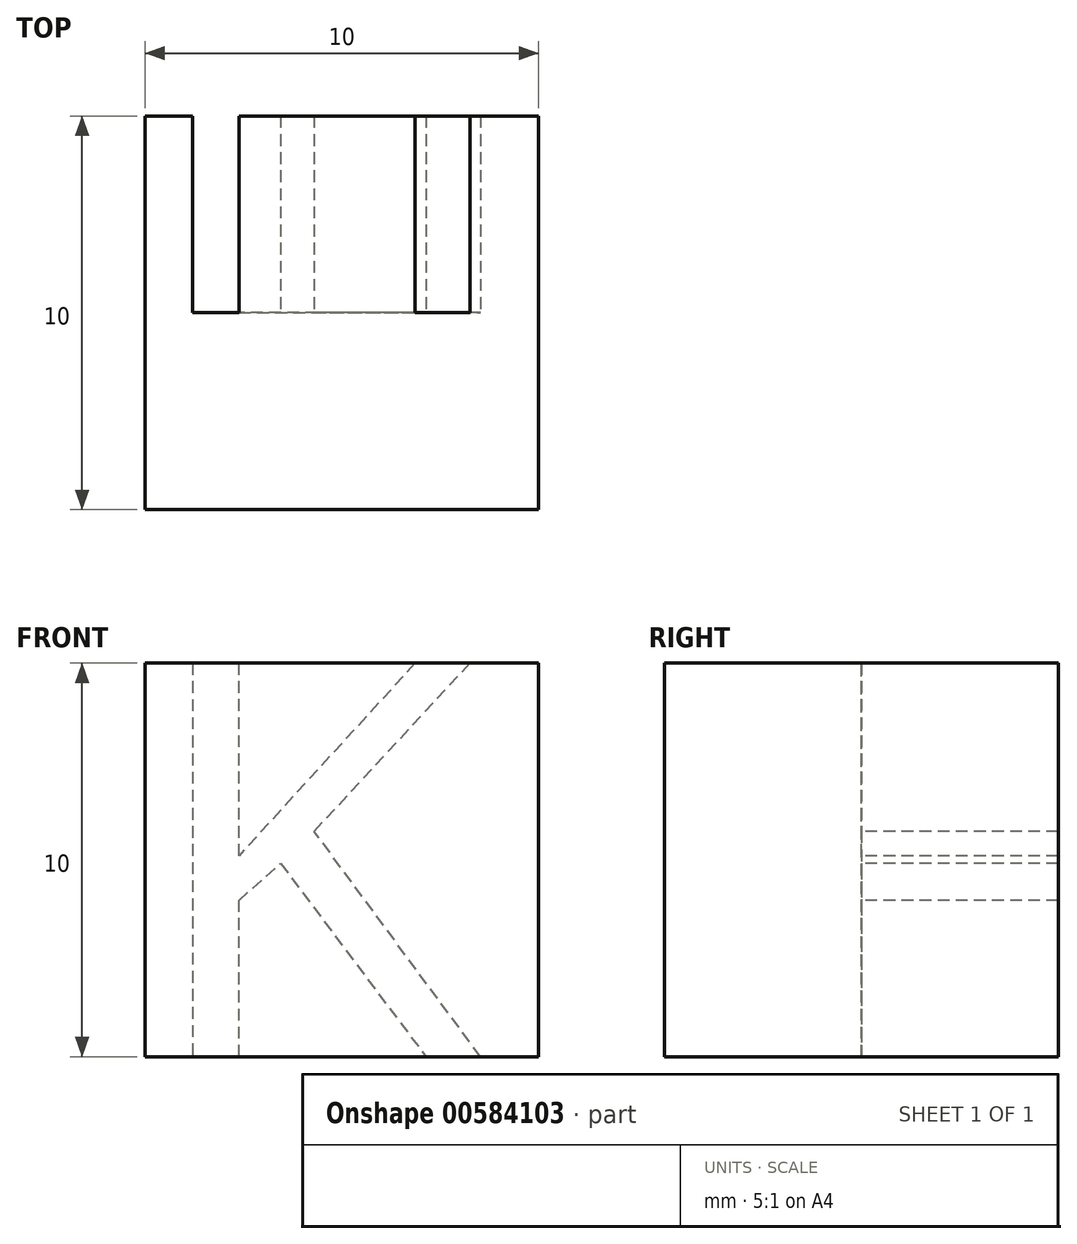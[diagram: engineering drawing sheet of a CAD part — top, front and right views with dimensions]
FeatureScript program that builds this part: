
annotation { "Feature Type Name" : "Feature", "Feature Type Description" : "" }
export const myFeature = defineFeature(function(context is Context, id is Id, definition is map)
    precondition{}
    {
        {
            var Q0;
            Q0=qCreatedBy(makeId("Top.planeOp"),FACE);
            var sketch = newSketch(context, id + "F0", { "sketchPlane" : qUnion([Q0])});
            skLineSegment(sketch, "E0.rect.bottom", {"start": v(-5, 5) * mm, "end": v(5, 5) * mm});
            skLineSegment(sketch, "E0.rect.top", {"start": v(-5, -5) * mm, "end": v(5, -5) * mm});
            skLineSegment(sketch, "E0.rect.left", {"start": v(-5, 5) * mm, "end": v(-5, -5) * mm});
            skLineSegment(sketch, "E0.rect.right", {"start": v(5, 5) * mm, "end": v(5, -5) * mm});
            skPoint(sketch, "E0.rect.middle", {"position": v(0, 0) * mm});
            skSolve(sketch);
        }
        {
            var Q0;
            Q0=qSketchRegion(id+"F0",true);
            extrude(context, id + "F1", {"entities" : qUnion([Q0]), "depth" : 10 * mm});
        }
        {
            var Q0;
            Q0=qCreatedBy(makeId("Front.planeOp"),FACE);
            var sketch = newSketch(context, id + "F2", { "sketchPlane" : qUnion([Q0])});
            skText(sketch, "E1", { "text": "K", "fontName": "OpenSans-Regular.ttf"});
            const initialGuessF2  = {"E1": [-0.00518, 0, 1, 0, 0.01021]};
            skSetInitialGuess(sketch, initialGuessF2);
            skSolve(sketch);
        }
        {
            var Q0;
            Q0 = qSketchRegion(id + "F2", true);
            extrude(context, id + "F3", {"entities" : qUnion([Q0]), "operationType" : NewBodyOperationType.REMOVE, "oppositeDirection" : true, "depth" : 25.4 * mm, "offsetDistance" : 25 * mm});
        }
    });
